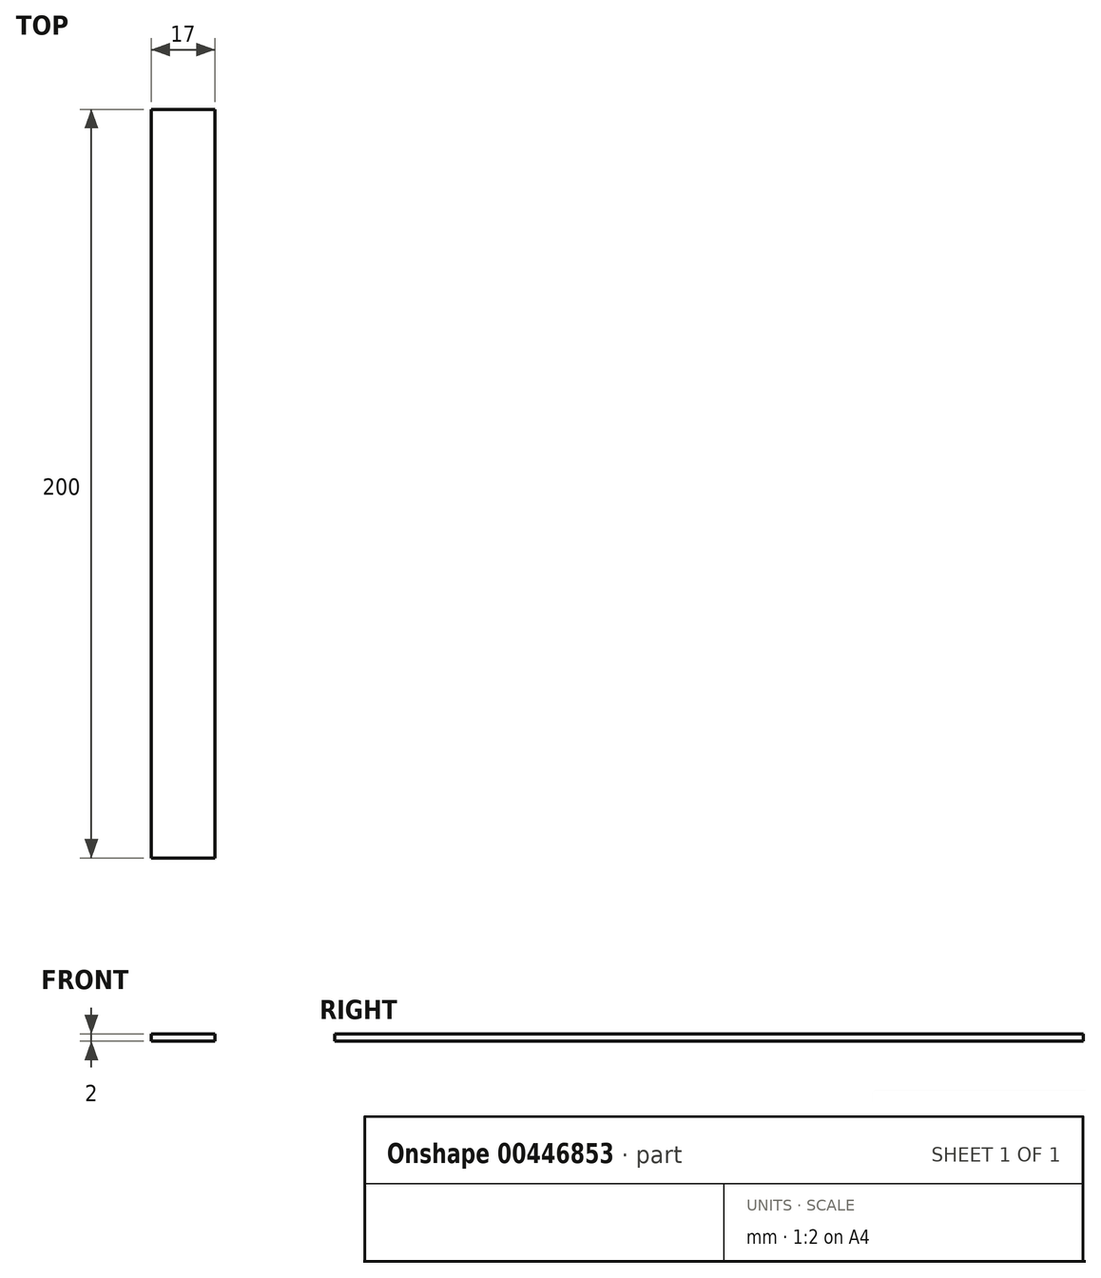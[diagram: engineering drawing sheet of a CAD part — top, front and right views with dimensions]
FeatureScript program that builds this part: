
annotation { "Feature Type Name" : "Feature", "Feature Type Description" : "" }
export const myFeature = defineFeature(function(context is Context, id is Id, definition is map)
    precondition{}
    {
        {
            var Q0;
            Q0=qCreatedBy(makeId("Front.planeOp"),FACE);
            var sketch = newSketch(context, id + "F0", { "sketchPlane" : qUnion([Q0])});
            skLineSegment(sketch, "E0.bottom", {"start": v(0, 0) * mm, "end": v(17, 0) * mm});
            skLineSegment(sketch, "E0.top", {"start": v(0, 2) * mm, "end": v(17, 2) * mm});
            skLineSegment(sketch, "E0.left", {"start": v(0, 0) * mm, "end": v(0, 2) * mm});
            skLineSegment(sketch, "E0.right", {"start": v(17, 0) * mm, "end": v(17, 2) * mm});
            skLineSegment(sketch, "E1.bottom", {"start": v(3.2, 2) * mm, "end": v(4, 2) * mm});
            skLineSegment(sketch, "E1.top", {"start": v(3.2, 4.03) * mm, "end": v(4, 4.03) * mm});
            skLineSegment(sketch, "E1.left", {"start": v(3.2, 2) * mm, "end": v(3.2, 4.03) * mm});
            skLineSegment(sketch, "E1.right", {"start": v(4, 2) * mm, "end": v(4, 4.03) * mm});
            skLineSegment(sketch, "E2.bottom", {"start": v(13, 2) * mm, "end": v(13.8, 2) * mm});
            skLineSegment(sketch, "E2.top", {"start": v(13, 4.03) * mm, "end": v(13.8, 4.03) * mm});
            skLineSegment(sketch, "E2.left", {"start": v(13, 2) * mm, "end": v(13, 4.03) * mm});
            skLineSegment(sketch, "E2.right", {"start": v(13.8, 2) * mm, "end": v(13.8, 4.03) * mm});
            skSolve(sketch);
        }
        {
            var Q0;
            Q0=makeQuery(id+"F0.imprint","IMPRINT",FACE,{"disambiguationData":[TD([[makeQuery(id+"F0.imprint","IMPRINT",EDGE,{"derivedFrom":sQuery(id+"F0.wireOp",EDGE,"E0.bottom")}),1.0]])]});
            var Q1;
            Q1=makeQuery(id+"F0.imprint","IMPRINT",FACE,{"disambiguationData":[TD([[makeQuery(id+"F0.imprint","IMPRINT",EDGE,{"derivedFrom":sQuery(id+"F0.wireOp",EDGE,"E1.bottom")}),1.0]])]});
            var Q2;
            Q2=makeQuery(id+"F0.imprint","IMPRINT",FACE,{"disambiguationData":[TD([[makeQuery(id+"F0.imprint","IMPRINT",EDGE,{"derivedFrom":sQuery(id+"F0.wireOp",EDGE,"E2.bottom")}),1.0]])]});
            extrude(context, id + "F1", {"entities" : qUnion([Q0, Q1, Q2]), "depth" : 200 * mm});
        }
    });
